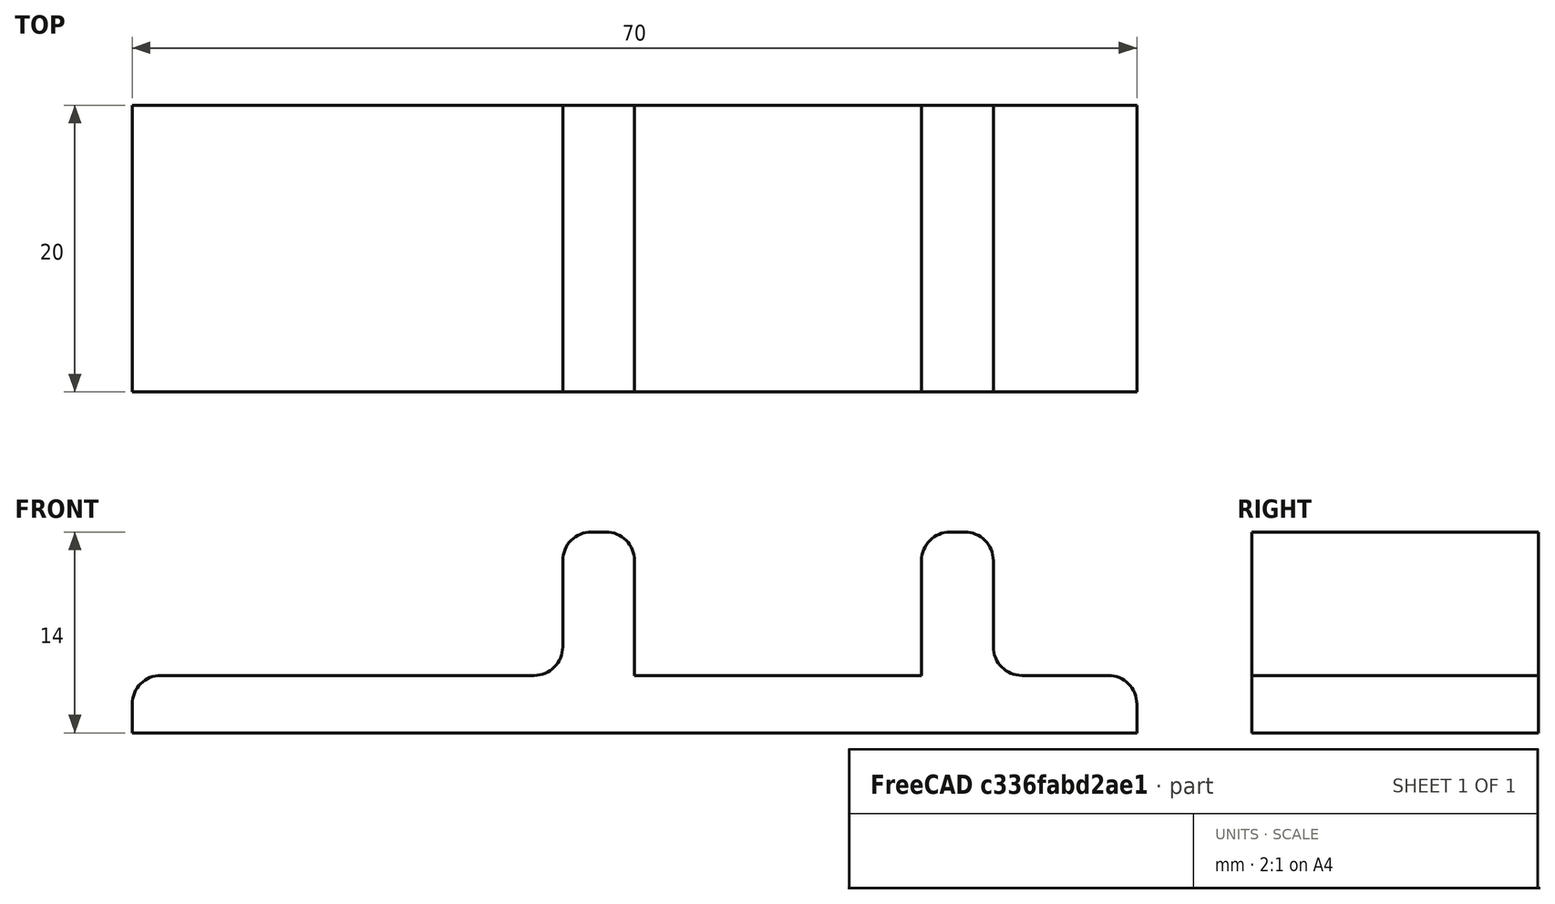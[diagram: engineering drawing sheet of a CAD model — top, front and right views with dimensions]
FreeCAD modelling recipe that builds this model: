
FCSTD DOCUMENT  (FreeCAD 0.18.4R)
Label: picture_stand
License: All rights reserved
LicenseURL: http://en.wikipedia.org/wiki/All_rights_reserved
objects: Part::Box×3, Part::MultiFuse×1, Part::Cut×1, Part::Fillet×1, App::Part×1, Spreadsheet::Sheet×1
note: 6 computed .brp shape members not serialized (recipe doc carries the construction recipe); baked Part::Feature solids carry a one-line shape summary decoded from their .brp

FEATURE [Part::Box] Box  label="Cube"
  AttacherType = Attacher::AttachEngine3D
  Height = 4
  Length = 70
  Width = 20
  expr: Width = p.width
  expr: Length = p.length
FEATURE [Part::Box] Box001  label="Cube001"
  AttacherType = Attacher::AttachEngine3D
  Height = 10
  Length = 30
  Placement = pos=(30,0,4) rot=(0,0,1;0rad)
  Width = 20
  expr: Width = p.width
FEATURE [Part::Box] Box002  label="Cube002"
  AttacherType = Attacher::AttachEngine3D
  Height = 10
  Length = 20
  Placement = pos=(35,0,4) rot=(0,0,1;0rad)
  Width = 20
  expr: Width = p.width
FEATURE [Part::MultiFuse] Fusion
  Shapes = -> [Box,Box001]
FEATURE [Part::Cut] Cut
  Base = -> Fusion
  Tool = -> Box002
FEATURE [Part::Fillet] Fillet
  Base = -> Cut
  Edges = 8 edges r=2: [Edge2,Edge13,Edge21,Edge30,Edge31,Edge38,Edge39,Edge40]
FEATURE [App::Part] Part
  Group = -> [Box,Box001,Box002,Fusion,Cut,Fillet]
  Origin = -> Origin
FEATURE [Spreadsheet::Sheet] Spreadsheet  label="p"
  cells = A1=width; B1(width)=20; A2=length; B2(length)=70
